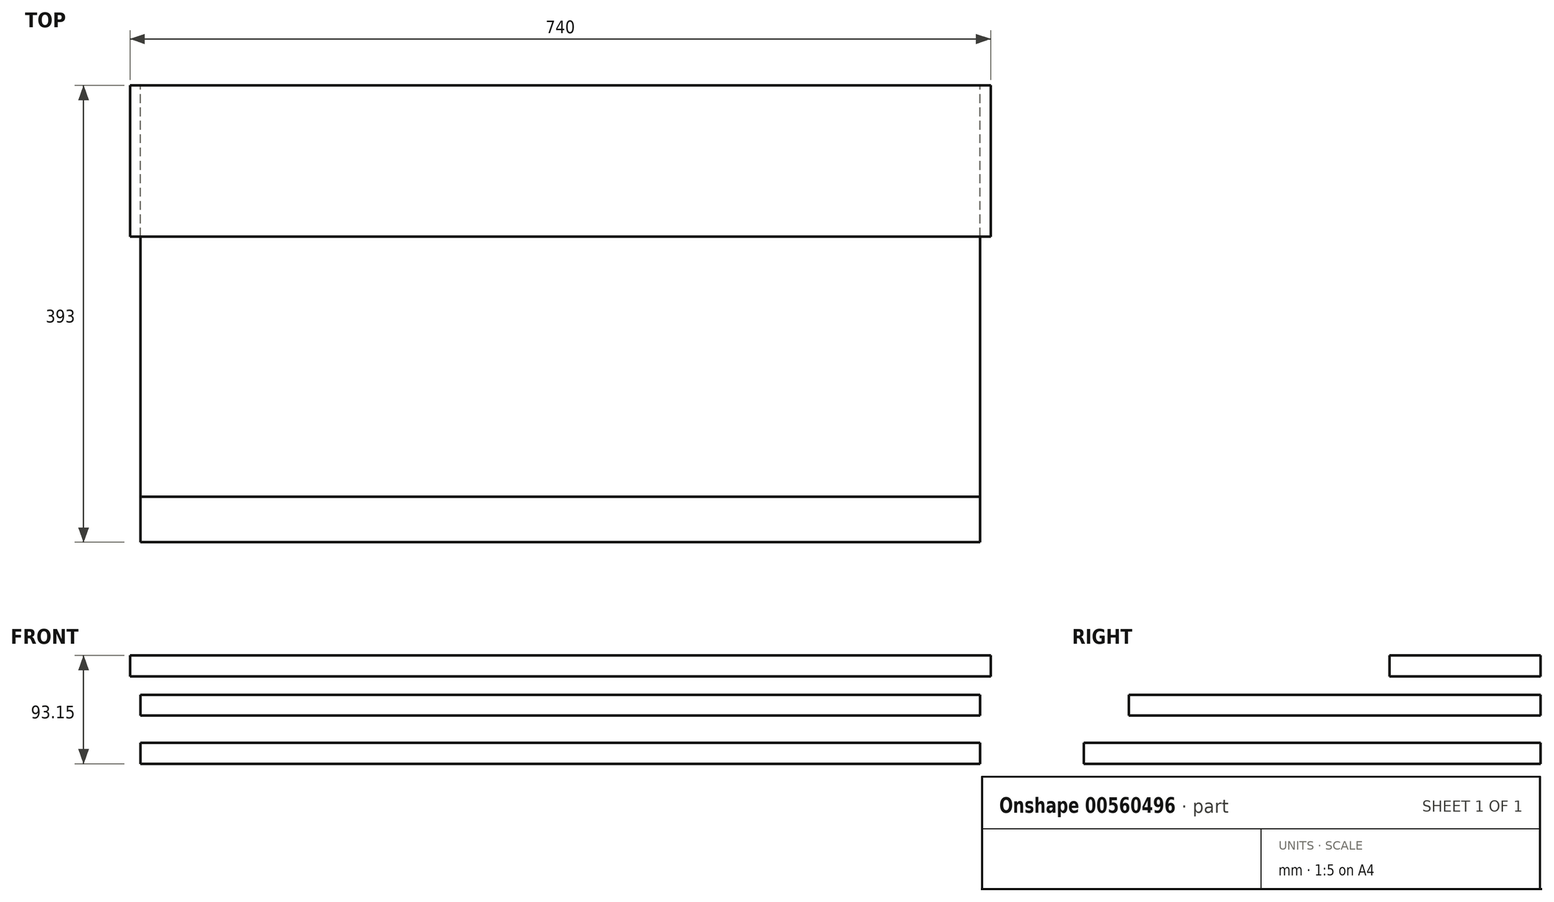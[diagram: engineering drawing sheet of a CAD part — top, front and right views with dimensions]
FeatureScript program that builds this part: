
annotation { "Feature Type Name" : "Feature", "Feature Type Description" : "" }
export const myFeature = defineFeature(function(context is Context, id is Id, definition is map)
    precondition{}
    {
        {
            var Q0;
            Q0=qCreatedBy(makeId("Front.planeOp"),FACE);
            var sketch = newSketch(context, id + "F0", { "sketchPlane" : qUnion([Q0])});
            skLineSegment(sketch, "E0.bottom", {"start": v(361, -32.37) * mm, "end": v(-361, -32.37) * mm});
            skLineSegment(sketch, "E0.top", {"start": v(361, -50.37) * mm, "end": v(-361, -50.37) * mm});
            skLineSegment(sketch, "E0.left", {"start": v(361, -32.37) * mm, "end": v(361, -50.37) * mm});
            skLineSegment(sketch, "E0.right", {"start": v(-361, -32.37) * mm, "end": v(-361, -50.37) * mm});
            skPoint(sketch, "E0.middle", {"position": v(0, -41.37) * mm});
            skLineSegment(sketch, "E1.bottom", {"start": v(361, 9) * mm, "end": v(-361, 9) * mm});
            skLineSegment(sketch, "E1.top", {"start": v(361, -9) * mm, "end": v(-361, -9) * mm});
            skLineSegment(sketch, "E1.left", {"start": v(361, 9) * mm, "end": v(361, -9) * mm});
            skLineSegment(sketch, "E1.right", {"start": v(-361, 9) * mm, "end": v(-361, -9) * mm});
            skPoint(sketch, "E1.middle", {"position": v(0, 0) * mm});
            skSolve(sketch);
        }
        {
            var Q0;
            Q0=makeQuery(id+"F0.imprint","IMPRINT",FACE,{"disambiguationData":[TD([[makeQuery(id+"F0.imprint","IMPRINT",EDGE,{"derivedFrom":sQuery(id+"F0.wireOp",EDGE,"E0.bottom")}),1.0]])]});
            extrude(context, id + "F1", {"entities" : qUnion([Q0]), "depth" : 393 * mm, "offsetDistance" : 25 * mm});
        }
        {
            var Q0;
            Q0=makeQuery(id+"F0.imprint","IMPRINT",FACE,{"disambiguationData":[TD([[makeQuery(id+"F0.imprint","IMPRINT",EDGE,{"derivedFrom":sQuery(id+"F0.wireOp",EDGE,"E1.bottom")}),1.0]])]});
            extrude(context, id + "F2", {"entities" : qUnion([Q0]), "depth" : 354 * mm, "offsetDistance" : 25 * mm});
        }
        {
            var Q0;
            Q0=qCreatedBy(makeId("Front.planeOp"),FACE);
            var sketch = newSketch(context, id + "F3", { "sketchPlane" : qUnion([Q0])});
            skLineSegment(sketch, "E2.bottom", {"start": v(370, 42.78) * mm, "end": v(-370, 42.78) * mm});
            skLineSegment(sketch, "E2.top", {"start": v(370, 24.78) * mm, "end": v(-370, 24.78) * mm});
            skLineSegment(sketch, "E2.left", {"start": v(370, 42.78) * mm, "end": v(370, 24.78) * mm});
            skLineSegment(sketch, "E2.right", {"start": v(-370, 42.78) * mm, "end": v(-370, 24.78) * mm});
            skPoint(sketch, "E2.middle", {"position": v(0, 33.78) * mm});
            skSolve(sketch);
        }
        {
            var Q0;
            Q0=makeQuery(id+"F3.imprint","IMPRINT",FACE,{"disambiguationData":[TD([[makeQuery(id+"F3.imprint","IMPRINT",EDGE,{"derivedFrom":sQuery(id+"F3.wireOp",EDGE,"E2.bottom")}),1.0]])]});
            extrude(context, id + "F4", {"entities" : qUnion([Q0]), "depth" : 130 * mm, "offsetDistance" : 25 * mm});
        }
    });
